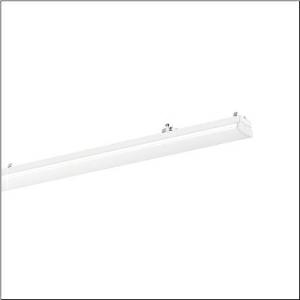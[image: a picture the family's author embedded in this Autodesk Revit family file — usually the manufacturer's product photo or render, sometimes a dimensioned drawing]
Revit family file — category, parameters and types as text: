
# Revit family: licross_21_recessed_opal_mo_52te1dmn4axg
name_source: partatom
category: Lighting Fixtures
units: mm (PartAtom-declared; Revit-internal decimal feet)

## family parameters
Cut with Voids When Loaded = No
Host = Face
Light Source = No
Part Type = Normal
Room Calculation Point = No
Round Connector Dimension = Use Diameter
Shared = No

## types (1)
- --- (1 x LED, 10420 lm, 60.5 W, 4000K)
    Apparent Load = 61 VA
    CIE Flux Codes = 44 73 91 87 100
    Color Rendering = 80
    Color Temperature = 4000K
    Default Elevation = 1800 mm
    Description = Licross 21 recessed opal MO, luminaire insert, of sheet steel, galvanised, coil coated, white, length: 1.500mm, width: 66mm, height: 67mm, LED rated luminous flux: 10.420lm, light colour: 840, SDCM (Standard Deviation of Colour Matching)MacAdam ≤ 3 SDCM (initial), control gear: ON/OFF Multilumen, with plug, 3-pole, with phase selection, mains connection: 220..240V, AC, 50/60Hz, rated input power: 61W, internal wiring halogen-free, primary optical cover: cover, of PMMA, light emission: direct with ceiling illumination distribution, primary light characteristic: symmetric, protection rating (complete): IP54, insulation class (complete): insulation class I (protective earthing), certification: CE, ENEC, VDE, UKCA, protection symbol: D if used in an environment with non-conductive dust loads with corresponding accessories, impact resistance: IK06, permissible ambient temperature for indoor applications: -35..+40°C, corresponds to IFS (International Featured Standards) requirements for safety and quality in the food industry, reducing of maximum allowable ambient temperature of 5°C with ceiling mounting, LABS conformity tested according to VDMA 24364:2018-05, The light source and the operating device comply with the requirements of the Ecodesign Regulation (EU) 2019/2020 and are replaceable in accordance with this regulation, packaging unit: 1 piece
    Height = 83 mm
    Lamp = 1 x LED
    Lamp Light Flux = 10420 lm
    Lamp Power = 60.5 W
    Lamp count = 1
    Length = 1500 mm
    Luminous efficacy = 172 lm/W
    Manufacturer = Siteco
    ModVariant = No
    Model = 52TE1DMN4AXG
    Mounting Place = Ceiling
    Mounting Type = Pendant
    Number of Poles = 1
    OnlyDefault = Yes
    Power Factor = 1
    Product Name = Licross 21 recessed opal MO
    Product group = luminaire insert | ceiling pendant
    ProductGroupID = 901
    Protection Class = Protection class I
    Protection Degree = IP 54
    RLX_Detail_Level = 1
    RLX_Emergency_Light_Flux = 0 lm
    RLX_Emergency_Type = 0
    RLX_Emergency_Type_DB = No
    RlxData = <blob elided: 25077 chars, md5=c890cfd0>
    Socket = socket
    Standby Power = 0 W
    System Light Flux = 10420 lm
    System Power = 61 W
    Type Comments = factory setting: luminous flux: 100 % | (A | C | E) | 140 mA
    Type Image = l_1313666.jpg
    URL = http://relux.com
    VarID = @adj_072309
    Voltage = 0 V
    Weight = 0.00 kg
    Width = 76 mm

## geometry (parser evidence)
native form markers: Blend x4, Sweep x12
no freeform markers — native parametric forms only
